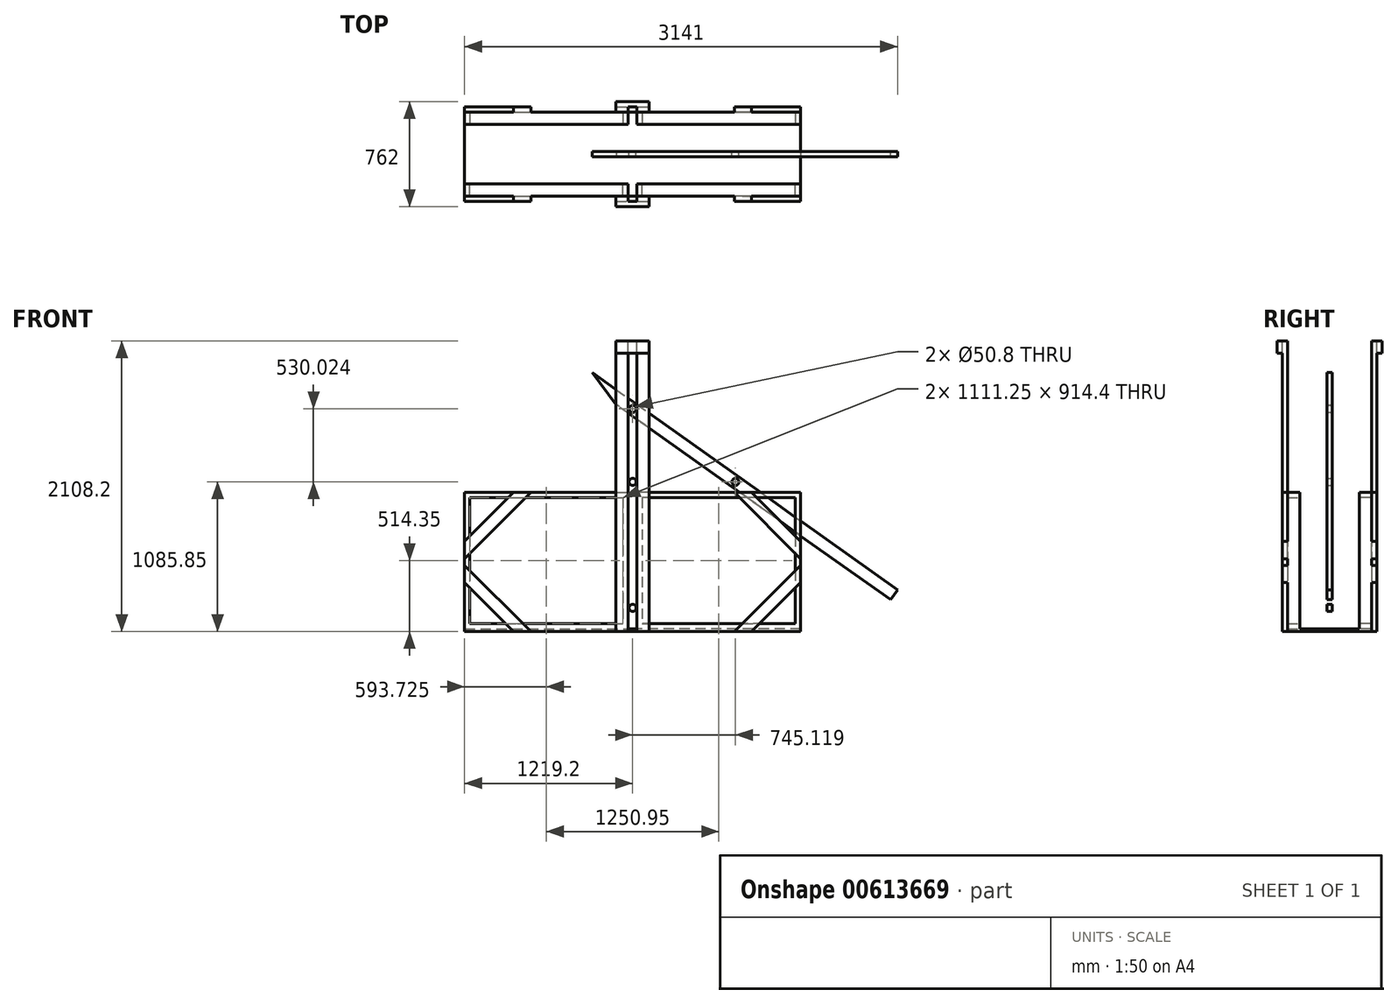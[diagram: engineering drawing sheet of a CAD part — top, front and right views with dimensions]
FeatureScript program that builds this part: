
annotation { "Feature Type Name" : "Feature", "Feature Type Description" : "" }
export const myFeature = defineFeature(function(context is Context, id is Id, definition is map)
    precondition{}
    {
        {
            var Q0;
            Q0=qCreatedBy(makeId("Top.planeOp"),FACE);
            var sketch = newSketch(context, id + "F0", { "sketchPlane" : qUnion([Q0])});
            skLineSegment(sketch, "E0.bottom", {"start": v(0, 0) * mm, "end": v(2438.4, 0) * mm});
            skLineSegment(sketch, "E0.top", {"start": v(0, -609.6) * mm, "end": v(2438.4, -609.6) * mm});
            skLineSegment(sketch, "E0.left", {"start": v(0, 0) * mm, "end": v(0, -609.6) * mm});
            skLineSegment(sketch, "E0.right", {"start": v(2438.4, 0) * mm, "end": v(2438.4, -609.6) * mm});
            skSolve(sketch);
        }
        {
            var Q0;
            Q0=qSketchRegion(id+"F0",true);
            extrude(context, id + "F1", {"entities" : qUnion([Q0]), "depth" : 19.05 * mm, "offsetDistance" : 25.4 * mm});
        }
        {
            var Q0;
            Q0=makeQuery(id+"F1.opExtrude","CAP_FACE",FACE,{"disambiguationData":[OSD([sQuery(id+"F0.wireOp",EDGE,"E0.bottom"),sQuery(id+"F0.wireOp",EDGE,"E0.top"),sQuery(id+"F0.wireOp",EDGE,"E0.left"),sQuery(id+"F0.wireOp",EDGE,"E0.right")])],"isStart":false});
            var sketch = newSketch(context, id + "F2", { "sketchPlane" : qUnion([Q0])});
            skLineSegment(sketch, "E1.bottom", {"start": v(0, 0) * mm, "end": v(1187.45, 0) * mm});
            skLineSegment(sketch, "E1.top", {"start": v(0, -88.9) * mm, "end": v(1187.45, -88.9) * mm});
            skLineSegment(sketch, "E1.left", {"start": v(0, 0) * mm, "end": v(0, -88.9) * mm});
            skLineSegment(sketch, "E1.right", {"start": v(1187.45, 0) * mm, "end": v(1187.45, -88.9) * mm});
            skLineSegment(sketch, "E2", {"start": v(0, -304.8) * mm, "end": v(2438.4, -304.8) * mm, "construction": true});
            skLineSegment(sketch, "E3", {"start": v(1219.2, 0) * mm, "end": v(1219.2, -609.6) * mm, "construction": true});
            skLineSegment(sketch, "E4.MirrorCS", {"start": v(2438.4, -88.9) * mm, "end": v(1250.95, -88.9) * mm});
            skLineSegment(sketch, "E5.MirrorCS", {"start": v(2438.4, 0) * mm, "end": v(1250.95, 0) * mm});
            skLineSegment(sketch, "E6.MirrorCS", {"start": v(1250.95, 0) * mm, "end": v(1250.95, -88.9) * mm});
            skLineSegment(sketch, "E7.MirrorCS", {"start": v(2438.4, 0) * mm, "end": v(2438.4, -88.9) * mm});
            skLineSegment(sketch, "E8.MirrorCS", {"start": v(1187.45, -609.6) * mm, "end": v(1187.45, -520.7) * mm});
            skLineSegment(sketch, "E9.MirrorCS", {"start": v(0, -609.6) * mm, "end": v(1187.45, -609.6) * mm});
            skLineSegment(sketch, "E10.MirrorCS", {"start": v(0, -520.7) * mm, "end": v(1187.45, -520.7) * mm});
            skLineSegment(sketch, "E11.MirrorCS", {"start": v(0, -609.6) * mm, "end": v(0, -520.7) * mm});
            skLineSegment(sketch, "E12.MirrorCS", {"start": v(1250.95, -609.6) * mm, "end": v(1250.95, -520.7) * mm});
            skLineSegment(sketch, "E13.MirrorCS", {"start": v(2438.4, -520.7) * mm, "end": v(1250.95, -520.7) * mm});
            skLineSegment(sketch, "E14.MirrorCS", {"start": v(2438.4, -609.6) * mm, "end": v(1250.95, -609.6) * mm});
            skLineSegment(sketch, "E15.MirrorCS", {"start": v(2438.4, -609.6) * mm, "end": v(2438.4, -520.7) * mm});
            skSolve(sketch);
        }
        {
            var Q0;
            Q0=qSketchRegion(id+"F2",true);
            extrude(context, id + "F3", {"entities" : qUnion([Q0]), "operationType" : NewBodyOperationType.ADD, "depth" : 38.1 * mm, "offsetDistance" : 25.4 * mm});
        }
        {
            var Q0;
            Q0=makeQuery(id+"F3.opExtrude","CAP_FACE",FACE,{"disambiguationData":[OSD([sQuery(id+"F2.wireOp",EDGE,"E1.bottom"),sQuery(id+"F2.wireOp",EDGE,"E1.top"),sQuery(id+"F2.wireOp",EDGE,"E1.left"),sQuery(id+"F2.wireOp",EDGE,"E1.right")])],"isStart":false});
            var sketch = newSketch(context, id + "F4", { "sketchPlane" : qUnion([Q0])});
            skLineSegment(sketch, "E16.bottom", {"start": v(0, 0) * mm, "end": v(38.1, 0) * mm});
            skLineSegment(sketch, "E16.top", {"start": v(0, -88.9) * mm, "end": v(38.1, -88.9) * mm});
            skLineSegment(sketch, "E16.left", {"start": v(0, 0) * mm, "end": v(0, -88.9) * mm});
            skLineSegment(sketch, "E16.right", {"start": v(38.1, 0) * mm, "end": v(38.1, -88.9) * mm});
            skLineSegment(sketch, "E17", {"start": v(0, -304.8) * mm, "end": v(2443.7, -304.8) * mm, "construction": true});
            skLineSegment(sketch, "E18", {"start": v(1219.2, 0) * mm, "end": v(1219.2, -609.6) * mm, "construction": true});
            skLineSegment(sketch, "E19", {"start": v(593.73, 0) * mm, "end": v(593.73, -88.9) * mm, "construction": true});
            skLineSegment(sketch, "E20.MirrorCS", {"start": v(1149.35, 0) * mm, "end": v(1149.35, -88.9) * mm});
            skLineSegment(sketch, "E21.MirrorCS", {"start": v(1187.45, 0) * mm, "end": v(1149.35, 0) * mm});
            skLineSegment(sketch, "E22.MirrorCS", {"start": v(1187.45, 0) * mm, "end": v(1187.45, -88.9) * mm});
            skLineSegment(sketch, "E23.MirrorCS", {"start": v(1187.45, -88.9) * mm, "end": v(1149.35, -88.9) * mm});
            skLineSegment(sketch, "E24.MirrorCS", {"start": v(1187.45, -609.6) * mm, "end": v(1187.45, -520.7) * mm});
            skLineSegment(sketch, "E25.MirrorCS", {"start": v(1187.45, -609.6) * mm, "end": v(1149.35, -609.6) * mm});
            skLineSegment(sketch, "E26.MirrorCS", {"start": v(1149.35, -609.6) * mm, "end": v(1149.35, -520.7) * mm});
            skLineSegment(sketch, "E27.MirrorCS", {"start": v(1187.45, -520.7) * mm, "end": v(1149.35, -520.7) * mm});
            skLineSegment(sketch, "E28.MirrorCS", {"start": v(38.1, -609.6) * mm, "end": v(38.1, -520.7) * mm});
            skLineSegment(sketch, "E29.MirrorCS", {"start": v(0, -609.6) * mm, "end": v(38.1, -609.6) * mm});
            skLineSegment(sketch, "E30.MirrorCS", {"start": v(0, -609.6) * mm, "end": v(0, -520.7) * mm});
            skLineSegment(sketch, "E31.MirrorCS", {"start": v(0, -520.7) * mm, "end": v(38.1, -520.7) * mm});
            skLineSegment(sketch, "E32.MirrorCS", {"start": v(1250.95, 0) * mm, "end": v(1250.95, -88.9) * mm});
            skLineSegment(sketch, "E33.MirrorCS", {"start": v(1250.95, 0) * mm, "end": v(1289.05, 0) * mm});
            skLineSegment(sketch, "E34.MirrorCS", {"start": v(1289.05, 0) * mm, "end": v(1289.05, -88.9) * mm});
            skLineSegment(sketch, "E35.MirrorCS", {"start": v(1250.95, -88.9) * mm, "end": v(1289.05, -88.9) * mm});
            skLineSegment(sketch, "E36.MirrorCS", {"start": v(1250.95, -609.6) * mm, "end": v(1250.95, -520.7) * mm});
            skLineSegment(sketch, "E37.MirrorCS", {"start": v(1250.95, -520.7) * mm, "end": v(1289.05, -520.7) * mm});
            skLineSegment(sketch, "E38.MirrorCS", {"start": v(1289.05, -609.6) * mm, "end": v(1289.05, -520.7) * mm});
            skLineSegment(sketch, "E39.MirrorCS", {"start": v(1250.95, -609.6) * mm, "end": v(1289.05, -609.6) * mm});
            skLineSegment(sketch, "E40.MirrorCS", {"start": v(2438.4, -609.6) * mm, "end": v(2400.3, -609.6) * mm});
            skLineSegment(sketch, "E41.MirrorCS", {"start": v(2438.4, -609.6) * mm, "end": v(2438.4, -520.7) * mm});
            skLineSegment(sketch, "E42.MirrorCS", {"start": v(2438.4, -520.7) * mm, "end": v(2400.3, -520.7) * mm});
            skLineSegment(sketch, "E43.MirrorCS", {"start": v(2400.3, -609.6) * mm, "end": v(2400.3, -520.7) * mm});
            skLineSegment(sketch, "E44.MirrorCS", {"start": v(2438.4, -88.9) * mm, "end": v(2400.3, -88.9) * mm});
            skLineSegment(sketch, "E45.MirrorCS", {"start": v(2438.4, 0) * mm, "end": v(2400.3, 0) * mm});
            skLineSegment(sketch, "E46.MirrorCS", {"start": v(2438.4, 0) * mm, "end": v(2438.4, -88.9) * mm});
            skLineSegment(sketch, "E47.MirrorCS", {"start": v(2400.3, 0) * mm, "end": v(2400.3, -88.9) * mm});
            skSolve(sketch);
        }
        {
            var Q0;
            Q0=qSketchRegion(id+"F4",true);
            extrude(context, id + "F5", {"entities" : qUnion([Q0]), "operationType" : NewBodyOperationType.ADD, "depth" : 914.4 * mm, "offsetDistance" : 25.4 * mm});
        }
        {
            var Q0;
            Q0=makeQuery(id+"F5.opExtrude","CAP_FACE",FACE,{"disambiguationData":[OSD([sQuery(id+"F4.wireOp",EDGE,"E16.bottom"),sQuery(id+"F4.wireOp",EDGE,"E16.top"),sQuery(id+"F4.wireOp",EDGE,"E16.left"),sQuery(id+"F4.wireOp",EDGE,"E16.right")])],"isStart":false});
            var sketch = newSketch(context, id + "F6", { "sketchPlane" : qUnion([Q0])});
            skLineSegment(sketch, "E48.bottom", {"start": v(0, 0) * mm, "end": v(1187.45, 0) * mm});
            skLineSegment(sketch, "E48.top", {"start": v(0, -88.9) * mm, "end": v(1187.45, -88.9) * mm});
            skLineSegment(sketch, "E48.left", {"start": v(0, 0) * mm, "end": v(0, -88.9) * mm});
            skLineSegment(sketch, "E48.right", {"start": v(1187.45, 0) * mm, "end": v(1187.45, -88.9) * mm});
            skLineSegment(sketch, "E49", {"start": v(0, -304.8) * mm, "end": v(2439.86, -304.8) * mm, "construction": true});
            skLineSegment(sketch, "E50", {"start": v(1219.2, 0) * mm, "end": v(1219.2, -609.6) * mm, "construction": true});
            skLineSegment(sketch, "E51.MirrorCS", {"start": v(2438.4, 0) * mm, "end": v(1250.95, 0) * mm});
            skLineSegment(sketch, "E52.MirrorCS", {"start": v(2438.4, -88.9) * mm, "end": v(1250.95, -88.9) * mm});
            skLineSegment(sketch, "E53.MirrorCS", {"start": v(2438.4, 0) * mm, "end": v(2438.4, -88.9) * mm});
            skLineSegment(sketch, "E54.MirrorCS", {"start": v(1250.95, 0) * mm, "end": v(1250.95, -88.9) * mm});
            skLineSegment(sketch, "E55.MirrorCS", {"start": v(2438.4, -520.7) * mm, "end": v(1250.95, -520.7) * mm});
            skLineSegment(sketch, "E56.MirrorCS", {"start": v(2438.4, -609.6) * mm, "end": v(1250.95, -609.6) * mm});
            skLineSegment(sketch, "E57.MirrorCS", {"start": v(1187.45, -609.6) * mm, "end": v(1187.45, -520.7) * mm});
            skLineSegment(sketch, "E58.MirrorCS", {"start": v(0, -609.6) * mm, "end": v(0, -520.7) * mm});
            skLineSegment(sketch, "E59.MirrorCS", {"start": v(0, -520.7) * mm, "end": v(1187.45, -520.7) * mm});
            skLineSegment(sketch, "E60.MirrorCS", {"start": v(2438.4, -609.6) * mm, "end": v(2438.4, -520.7) * mm});
            skLineSegment(sketch, "E61.MirrorCS", {"start": v(1250.95, -609.6) * mm, "end": v(1250.95, -520.7) * mm});
            skLineSegment(sketch, "E62.MirrorCS", {"start": v(0, -609.6) * mm, "end": v(1187.45, -609.6) * mm});
            skSolve(sketch);
        }
        {
            var Q0;
            Q0=qSketchRegion(id+"F6",true);
            extrude(context, id + "F7", {"entities" : qUnion([Q0]), "operationType" : NewBodyOperationType.ADD, "depth" : 38.1 * mm, "offsetDistance" : 25.4 * mm});
        }
        {
            var Q0;
            Q0=makeQuery(id+"F7.boolean.opBoolean","MERGE",FACE,{"derivedFrom":[makeQuery(id+"F5.boolean.opBoolean","MERGE",FACE,{"derivedFrom":[makeQuery(id+"F3.boolean.opBoolean","MERGE",FACE,{"derivedFrom":[makeQuery(id+"F1.opExtrude","SWEPT_FACE",FACE,{"disambiguationData":[OSD([sQuery(id+"F0.wireOp",EDGE,"E0.top")])]}),makeQuery(id+"F3.opExtrude","SWEPT_FACE",FACE,{"disambiguationData":[OSD([sQuery(id+"F2.wireOp",EDGE,"E9.MirrorCS")])]}),makeQuery(id+"F3.opExtrude","SWEPT_FACE",FACE,{"disambiguationData":[OSD([sQuery(id+"F2.wireOp",EDGE,"E14.MirrorCS")])]})]}),makeQuery(id+"F5.opExtrude","SWEPT_FACE",FACE,{"disambiguationData":[OSD([sQuery(id+"F4.wireOp",EDGE,"E25.MirrorCS")])]}),makeQuery(id+"F5.opExtrude","SWEPT_FACE",FACE,{"disambiguationData":[OSD([sQuery(id+"F4.wireOp",EDGE,"E29.MirrorCS")])]}),makeQuery(id+"F5.opExtrude","SWEPT_FACE",FACE,{"disambiguationData":[OSD([sQuery(id+"F4.wireOp",EDGE,"E39.MirrorCS")])]}),makeQuery(id+"F5.opExtrude","SWEPT_FACE",FACE,{"disambiguationData":[OSD([sQuery(id+"F4.wireOp",EDGE,"E40.MirrorCS")])]})]}),makeQuery(id+"F7.opExtrude","SWEPT_FACE",FACE,{"disambiguationData":[OSD([sQuery(id+"F6.wireOp",EDGE,"E56.MirrorCS")])]}),makeQuery(id+"F7.opExtrude","SWEPT_FACE",FACE,{"disambiguationData":[OSD([sQuery(id+"F6.wireOp",EDGE,"E62.MirrorCS")])]})]});
            var sketch = newSketch(context, id + "F8", { "sketchPlane" : qUnion([Q0])});
            skLineSegment(sketch, "E63.bottom", {"start": v(1250.95, 0) * mm, "end": v(1339.85, 0) * mm});
            skLineSegment(sketch, "E63.top", {"start": v(1250.95, 2108.2) * mm, "end": v(1339.85, 2108.2) * mm});
            skLineSegment(sketch, "E63.left", {"start": v(1250.95, 0) * mm, "end": v(1250.95, 2108.2) * mm});
            skLineSegment(sketch, "E63.right", {"start": v(1339.85, 0) * mm, "end": v(1339.85, 2108.2) * mm});
            skLineSegment(sketch, "E64", {"start": v(2082.8, 1009.65) * mm, "end": v(2438.4, 654.05) * mm});
            skLineSegment(sketch, "E65", {"start": v(2438.4, 654.05) * mm, "end": v(2438.4, 528.33) * mm});
            skLineSegment(sketch, "E66", {"start": v(2438.4, 528.33) * mm, "end": v(1957.08, 1009.65) * mm});
            skLineSegment(sketch, "E67", {"start": v(1957.08, 1009.65) * mm, "end": v(2082.8, 1009.65) * mm});
            skLineSegment(sketch, "E68", {"start": v(2438.4, 504.82) * mm, "end": v(0, 504.82) * mm, "construction": true});
            skLineSegment(sketch, "E69", {"start": v(1219.2, 0) * mm, "end": v(1219.2, 1299.12) * mm, "construction": true});
            skLineSegment(sketch, "E70.MirrorCS", {"start": v(2438.4, 481.32) * mm, "end": v(1957.08, 0) * mm});
            skLineSegment(sketch, "E71.MirrorCS", {"start": v(1957.08, 0) * mm, "end": v(2082.8, 0) * mm});
            skLineSegment(sketch, "E72.MirrorCS", {"start": v(2082.8, 0) * mm, "end": v(2438.4, 355.6) * mm});
            skLineSegment(sketch, "E73.MirrorCS", {"start": v(2438.4, 355.6) * mm, "end": v(2438.4, 481.32) * mm});
            skLineSegment(sketch, "E74.MirrorCS", {"start": v(355.6, 0) * mm, "end": v(0, 355.6) * mm});
            skLineSegment(sketch, "E75.MirrorCS", {"start": v(481.32, 0) * mm, "end": v(355.6, 0) * mm});
            skLineSegment(sketch, "E76.MirrorCS", {"start": v(0, 481.32) * mm, "end": v(481.32, 0) * mm});
            skLineSegment(sketch, "E77.MirrorCS", {"start": v(355.6, 1009.65) * mm, "end": v(0, 654.05) * mm});
            skLineSegment(sketch, "E78.MirrorCS", {"start": v(481.32, 1009.65) * mm, "end": v(355.6, 1009.65) * mm});
            skLineSegment(sketch, "E79.MirrorCS", {"start": v(0, 355.6) * mm, "end": v(0, 481.32) * mm});
            skLineSegment(sketch, "E80.MirrorCS", {"start": v(0, 654.05) * mm, "end": v(0, 528.33) * mm});
            skLineSegment(sketch, "E81.MirrorCS", {"start": v(0, 528.33) * mm, "end": v(481.32, 1009.65) * mm});
            skLineSegment(sketch, "E82.MirrorCS", {"start": v(1187.45, 2108.2) * mm, "end": v(1098.55, 2108.2) * mm});
            skLineSegment(sketch, "E83.MirrorCS", {"start": v(1187.45, 0) * mm, "end": v(1187.45, 2108.2) * mm});
            skLineSegment(sketch, "E84.MirrorCS", {"start": v(1098.55, 0) * mm, "end": v(1098.55, 2108.2) * mm});
            skLineSegment(sketch, "E85.MirrorCS", {"start": v(1187.45, 0) * mm, "end": v(1098.55, 0) * mm});
            skLineSegment(sketch, "E86.MirrorCS", {"start": v(0, 504.82) * mm, "end": v(2438.4, 504.82) * mm, "construction": true});
            skSolve(sketch);
        }
        {
            var Q0;
            Q0=qSketchRegion(id+"F8",true);
            extrude(context, id + "F9", {"entities" : qUnion([Q0]), "operationType" : NewBodyOperationType.ADD, "depth" : 38.1 * mm, "offsetDistance" : 25.4 * mm});
        }
        {
            var Q0;
            Q0=makeQuery(id+"F7.boolean.opBoolean","MERGE",FACE,{"derivedFrom":[makeQuery(id+"F5.boolean.opBoolean","MERGE",FACE,{"derivedFrom":[makeQuery(id+"F3.boolean.opBoolean","MERGE",FACE,{"derivedFrom":[makeQuery(id+"F1.opExtrude","SWEPT_FACE",FACE,{"disambiguationData":[OSD([sQuery(id+"F0.wireOp",EDGE,"E0.bottom")])]}),makeQuery(id+"F3.opExtrude","SWEPT_FACE",FACE,{"disambiguationData":[OSD([sQuery(id+"F2.wireOp",EDGE,"E1.bottom")])]}),makeQuery(id+"F3.opExtrude","SWEPT_FACE",FACE,{"disambiguationData":[OSD([sQuery(id+"F2.wireOp",EDGE,"E5.MirrorCS")])]})]}),makeQuery(id+"F5.opExtrude","SWEPT_FACE",FACE,{"disambiguationData":[OSD([sQuery(id+"F4.wireOp",EDGE,"E16.bottom")])]}),makeQuery(id+"F5.opExtrude","SWEPT_FACE",FACE,{"disambiguationData":[OSD([sQuery(id+"F4.wireOp",EDGE,"E21.MirrorCS")])]}),makeQuery(id+"F5.opExtrude","SWEPT_FACE",FACE,{"disambiguationData":[OSD([sQuery(id+"F4.wireOp",EDGE,"E33.MirrorCS")])]}),makeQuery(id+"F5.opExtrude","SWEPT_FACE",FACE,{"disambiguationData":[OSD([sQuery(id+"F4.wireOp",EDGE,"E45.MirrorCS")])]})]}),makeQuery(id+"F7.opExtrude","SWEPT_FACE",FACE,{"disambiguationData":[OSD([sQuery(id+"F6.wireOp",EDGE,"E48.bottom")])]}),makeQuery(id+"F7.opExtrude","SWEPT_FACE",FACE,{"disambiguationData":[OSD([sQuery(id+"F6.wireOp",EDGE,"E51.MirrorCS")])]})]});
            var sketch = newSketch(context, id + "F10", { "sketchPlane" : qUnion([Q0])});
            skLineSegment(sketch, "E87.bottom", {"start": v(-1187.45, 0) * mm, "end": v(-1098.55, 0) * mm});
            skLineSegment(sketch, "E87.top", {"start": v(-1187.45, 2108.2) * mm, "end": v(-1098.55, 2108.2) * mm});
            skLineSegment(sketch, "E87.left", {"start": v(-1187.45, 0) * mm, "end": v(-1187.45, 2108.2) * mm});
            skLineSegment(sketch, "E87.right", {"start": v(-1098.55, 0) * mm, "end": v(-1098.55, 2108.2) * mm});
            skLineSegment(sketch, "E88", {"start": v(-355.6, 1009.65) * mm, "end": v(0, 654.05) * mm});
            skLineSegment(sketch, "E89", {"start": v(0, 654.05) * mm, "end": v(0, 528.33) * mm});
            skLineSegment(sketch, "E90", {"start": v(0, 528.33) * mm, "end": v(-481.32, 1009.65) * mm});
            skLineSegment(sketch, "E91", {"start": v(-481.32, 1009.65) * mm, "end": v(-355.6, 1009.65) * mm});
            skLineSegment(sketch, "E92", {"start": v(0, 504.83) * mm, "end": v(-2438.4, 504.82) * mm, "construction": true});
            skLineSegment(sketch, "E93", {"start": v(-1219.2, -181.13) * mm, "end": v(-1219.2, 1118) * mm, "construction": true});
            skLineSegment(sketch, "E94.MirrorCS", {"start": v(0, 481.32) * mm, "end": v(-481.32, 0) * mm});
            skLineSegment(sketch, "E95.MirrorCS", {"start": v(-481.32, 0) * mm, "end": v(-355.6, 0) * mm});
            skLineSegment(sketch, "E96.MirrorCS", {"start": v(-355.6, 0) * mm, "end": v(0, 355.6) * mm});
            skLineSegment(sketch, "E97.MirrorCS", {"start": v(0, 355.6) * mm, "end": v(0, 481.32) * mm});
            skLineSegment(sketch, "E98.MirrorCS", {"start": v(-2082.8, 0) * mm, "end": v(-2438.4, 355.6) * mm});
            skLineSegment(sketch, "E99.MirrorCS", {"start": v(-1957.08, 0) * mm, "end": v(-2082.8, 0) * mm});
            skLineSegment(sketch, "E100.MirrorCS", {"start": v(-2438.4, 481.32) * mm, "end": v(-1957.08, 0) * mm});
            skLineSegment(sketch, "E101.MirrorCS", {"start": v(-2082.8, 1009.65) * mm, "end": v(-2438.4, 654.05) * mm});
            skLineSegment(sketch, "E102.MirrorCS", {"start": v(-1957.08, 1009.65) * mm, "end": v(-2082.8, 1009.65) * mm});
            skLineSegment(sketch, "E103.MirrorCS", {"start": v(-2438.4, 355.6) * mm, "end": v(-2438.4, 481.32) * mm});
            skLineSegment(sketch, "E104.MirrorCS", {"start": v(-2438.4, 654.05) * mm, "end": v(-2438.4, 528.33) * mm});
            skLineSegment(sketch, "E105.MirrorCS", {"start": v(-2438.4, 528.33) * mm, "end": v(-1957.08, 1009.65) * mm});
            skLineSegment(sketch, "E106.MirrorCS", {"start": v(-1250.95, 2108.2) * mm, "end": v(-1339.85, 2108.2) * mm});
            skLineSegment(sketch, "E107.MirrorCS", {"start": v(-1250.95, 0) * mm, "end": v(-1250.95, 2108.2) * mm});
            skLineSegment(sketch, "E108.MirrorCS", {"start": v(-1339.85, 0) * mm, "end": v(-1339.85, 2108.2) * mm});
            skLineSegment(sketch, "E109.MirrorCS", {"start": v(-1250.95, 0) * mm, "end": v(-1339.85, 0) * mm});
            skLineSegment(sketch, "E110.MirrorCS", {"start": v(-2438.4, 504.82) * mm, "end": v(0, 504.83) * mm, "construction": true});
            skSolve(sketch);
        }
        {
            var Q0;
            Q0=qSketchRegion(id+"F10",true);
            extrude(context, id + "F11", {"entities" : qUnion([Q0]), "operationType" : NewBodyOperationType.ADD, "depth" : 38.1 * mm, "offsetDistance" : 25.4 * mm});
        }
        {
            var Q0;
            Q0=makeQuery(id+"F11.opExtrude","CAP_FACE",FACE,{"disambiguationData":[OSD([sQuery(id+"F10.wireOp",EDGE,"E106.MirrorCS"),sQuery(id+"F10.wireOp",EDGE,"E107.MirrorCS"),sQuery(id+"F10.wireOp",EDGE,"E108.MirrorCS"),sQuery(id+"F10.wireOp",EDGE,"E109.MirrorCS")])],"isStart":false});
            var sketch = newSketch(context, id + "F12", { "sketchPlane" : qUnion([Q0])});
            skLineSegment(sketch, "E111.bottom", {"start": v(-1339.85, 2108.2) * mm, "end": v(-1098.55, 2108.2) * mm});
            skLineSegment(sketch, "E111.top", {"start": v(-1339.85, 2019.3) * mm, "end": v(-1098.55, 2019.3) * mm});
            skLineSegment(sketch, "E111.left", {"start": v(-1339.85, 2108.2) * mm, "end": v(-1339.85, 2019.3) * mm});
            skLineSegment(sketch, "E111.right", {"start": v(-1098.55, 2108.2) * mm, "end": v(-1098.55, 2019.3) * mm});
            skSolve(sketch);
        }
        {
            var Q0;
            Q0=qSketchRegion(id+"F12",true);
            extrude(context, id + "F13", {"entities" : qUnion([Q0]), "operationType" : NewBodyOperationType.ADD, "depth" : 38.1 * mm, "offsetDistance" : 25.4 * mm});
        }
        {
            var Q0;
            Q0=makeQuery(id+"F9.opExtrude","CAP_FACE",FACE,{"disambiguationData":[OSD([sQuery(id+"F8.wireOp",EDGE,"E82.MirrorCS"),sQuery(id+"F8.wireOp",EDGE,"E83.MirrorCS"),sQuery(id+"F8.wireOp",EDGE,"E84.MirrorCS"),sQuery(id+"F8.wireOp",EDGE,"E85.MirrorCS")])],"isStart":false});
            var sketch = newSketch(context, id + "F14", { "sketchPlane" : qUnion([Q0])});
            skLineSegment(sketch, "E112.bottom", {"start": v(1098.55, 2108.2) * mm, "end": v(1339.85, 2108.2) * mm});
            skLineSegment(sketch, "E112.top", {"start": v(1098.55, 2019.3) * mm, "end": v(1339.85, 2019.3) * mm});
            skLineSegment(sketch, "E112.left", {"start": v(1098.55, 2108.2) * mm, "end": v(1098.55, 2019.3) * mm});
            skLineSegment(sketch, "E112.right", {"start": v(1339.85, 2108.2) * mm, "end": v(1339.85, 2019.3) * mm});
            skSolve(sketch);
        }
        {
            var Q0;
            Q0=qSketchRegion(id+"F14",true);
            extrude(context, id + "F15", {"entities" : qUnion([Q0]), "operationType" : NewBodyOperationType.ADD, "depth" : 38.1 * mm, "offsetDistance" : 25.4 * mm});
        }
        {
            var Q0;
            {var subQ1=sQuery(id+"F10.wireOp",EDGE,"E106.MirrorCS");var subQ2=sQuery(id+"F10.wireOp",EDGE,"E108.MirrorCS");var subQ4=sQuery(id+"F10.wireOp",EDGE,"E107.MirrorCS");Q0=makeQuery(id+"F11.boolean.opBoolean","SPLIT",FACE,{"disambiguationData":[TD([makeQuery(id+"F3.opExtrude","SWEPT_FACE",FACE,{"disambiguationData":[OSD([sQuery(id+"F2.wireOp",EDGE,"E6.MirrorCS")])]})])],"derivedFrom":makeQuery(id+"F11.opExtrude","CAP_FACE",FACE,{"disambiguationData":[OSD([subQ1,subQ4,subQ2,sQuery(id+"F10.wireOp",EDGE,"E109.MirrorCS")])],"isStart":true})});}
            cPlane(context, id + "F16", {"entities" : qUnion([Q0]), "cplaneType" : CPlaneType.OFFSET, "offset" : 304.8 * mm, "width" : 152.4 * mm, "height" : 152.4 * mm});
        }
        {
            var Q0;
            Q0=qCreatedBy(id+"F16.planeOp",FACE);
            var sketch = newSketch(context, id + "F17", { "sketchPlane" : qUnion([Q0])});
            skLineSegment(sketch, "E113", {"start": v(926.34, 1878.74) * mm, "end": v(3141, 303.4) * mm});
            skLineSegment(sketch, "E114", {"start": v(3141, 303.4) * mm, "end": v(3089.47, 230.95) * mm});
            skLineSegment(sketch, "E115", {"start": v(3089.47, 230.95) * mm, "end": v(1102.48, 1644.35) * mm});
            skLineSegment(sketch, "E116", {"start": v(1102.48, 1644.35) * mm, "end": v(926.34, 1878.74) * mm});
            skCircle(sketch, "E117", {"center": v(1219.2, 1615.87) * mm, "radius": 25.4 * mm});
            skCircle(sketch, "E118", {"center": v(1964.32, 1085.85) * mm, "radius": 25.4 * mm});
            skCircle(sketch, "E119", {"center": v(1219.2, 1085.85) * mm, "radius": 25.4 * mm});
            skLineSegment(sketch, "E120", {"start": v(1219.2, 0) * mm, "end": v(1219.2, 1933.95) * mm, "construction": true});
            skCircle(sketch, "E121", {"center": v(1219.2, 171.45) * mm, "radius": 25.4 * mm});
            skSolve(sketch);
        }
        {
            var Q0;
            Q0=qSketchRegion(id+"F17",true);
            extrude(context, id + "F18", {"entities" : qUnion([Q0]), "depth" : 38.1 * mm, "offsetDistance" : 25.4 * mm, "symmetric" : true});
        }
    });
